# Revit family: HI-MACS_CS454
name_source: partatom
category: Appareils sanitaires
revit_build: Autodesk Revit 2015 (Build: 20140606_1530(x64)
units: mm (PartAtom-declared; Revit-internal decimal feet)

## types (1)
- CS454
    Application = Kitchen (sinks) - Healthcare (sinks)
    BIMobject category = Basins
    Brand url = http://www.himacs.eu
    Date of publishing = 10/20/2017
    Description DEU = Verfügbar in Alpine White S028.
Garantie: HI-MACS® 15 Jahre.
Mit und ohne Überlauf. Unterhalb montiert.

Spülen aus HI-MACS® werden in einem hochwertigen Gussverfahren hergestellt. Ganz gleich, für welches Produkt aus dem umfangreichen Sortiment Sie sich entscheiden: Alle Spülen werden flächenbündig in die Arbeitsplatte eingesetzt bzw. untergebaut und sind optimal zu kombinieren. Darüber hinaus sind spezielle Maßanfertigungen möglich.
Bitte kontaktieren Sie uns, um weitere Informationen zu erhalten: www.himacs.eu
    Description ENG = Available in Alpine White S028.
Warranty: HI-MACS® 15 years.
With and without overflow. Under mounted.
HI-MACS® Sinks are produced using a high-quality casting technique. No matter which product you choose from our extensive, eminently combinable selection, all sinks are flush-mounted into the countertop or installed below the surface. Special custom-made creations are also an option.
Visit himacs.eu for more information.
    Description ESP = Disponible en Alpine White S028.
Garantia: HI-MACS® 15 años.
Con o sin rebosadero. Encastrar.
Los fregaderos de HI-MACS® se fabrican en un proceso de colado de alta calidad. No importa por qué producto se decida de la extensa gama: Todos los fregaderos se aplican enrasados en la encimera o instalados bajo encimera y se combinan óptimamente. Además, es posible realizarlos en medidas especiales.
Para obtener más información, visite himacs.eu.Disponible en Alpine White S028.
Garantia: HI-MACS® 15 años.
Con o sin rebosadero. Encastrar.
Los fregaderos de HI-MACS® se fabrican en un proceso de colado de alta calidad. No importa por qué producto se decida de la extensa gama: Todos los fregaderos se aplican enrasados en la encimera o instalados bajo encimera y se combinan óptimamente. Además, es posible realizarlos en medidas especiales.
Para obtener más información, visite himacs.eu.
    Description ITA = Disponibile in Alpine White S028.
Garanzia: HI-MACS® 15 anni.
Con o senza troppopieno. Installazione a filo al di sotto dei top.
I lavelli HI-MACS® sono prodotti utilizzando tecniche di colata di elevata qualità. A prescindere dal prodotto scelto dall’ampia selezione, perfetta per qualsiasi tipo di abbinamento, tutti i lavelli sono montati allo stesso livello del piano di lavoro oppure installati al di sotto della superficie. Sono altresì possibili soluzioni personalizzate su richiesta.
Per maggiori informazioni visitate il nostro sito internet himacs.eu Disponibile in Alpine White S028.
Garanzia: HI-MACS® 15 anni.
Con o senza troppopieno. Installazione a filo al di sotto dei top.
I lavelli HI-MACS® sono prodotti utilizzando tecniche di colata di elevata qualità. A prescindere dal prodotto scelto dall’ampia selezione, perfetta per qualsiasi tipo di abbinamento, tutti i lavelli sono montati allo stesso livello del piano di lavoro oppure installati al di sotto della superficie. Sono altresì possibili soluzioni personalizzate su richiesta.
Per maggiori informazioni visitate il nostro sito internet himacs.eu
    Design country = Italy
    Edition number = 1
    Elévation par défaut = 1219 mm
    Fabricant = HI-MACS
    Heigth = 180 mm  [stored 0.590551 ft]
    IFC Classification = Furnishing Element
    Length = 450 mm  [stored 1.47638 ft]
    Manufacturer country = Italy
    Manufacturer name = HI-MACS®
    Material main = Solid surface
    Material secondary = Natural Acrylic Stone
    Modèle = CS 454
    Mounting = Under Mounted
    NBS Reference Code = 35-65-70-94
    NBS Reference Description = Wash Basin Systems
    Nominal height = 400 mm  [stored 1.31234 ft]
    Nominal width = 450 mm  [stored 1.47638 ft]
    Product Guid = aa4f101a-b15d-4ea3-afbd-ea998ac4159d
    Product SKU = CS454
    Product certification = http://himacs.eu
    Product data url = https://bimobject.com
    Product family = Sinks, Baby Baths & Bowls
    Product group = Sinks
    Product url = http://himacs.eu
    QR code = http://bimobject.com
    Technical description = http://himacs.eu
    UNSPSC Code = 301815
    URL = http://himacs.eu
    Uniclass 1.4 Code = L7212
    Uniclass 1.4 Description = Washbasins
    Uniclass 2.0 Code = SS-35-65-70-94
    Uniclass 2.0 Description = Wash Basin Systems
    WASHBASIN MATERIAL = HI-MACS Natural Acrylic Stone
    Weight Net (Kg) = 9
    Weigth KG = 9
    Width = 400 mm  [stored 1.31234 ft]
    Youtube clip = https://www.youtube.com

note: [stored X ft] marks values corroborated as IEEE doubles in the binary element streams (Revit-internal decimal feet)
